annotation { "Feature Type Name" : "Feature", "Feature Type Description" : "" }
export const myFeature = defineFeature(function(context is Context, id is Id, definition is map)
    precondition{}
    {
        {
            var Q0;
            Q0=qCreatedBy(makeId("Top.planeOp"),FACE);
            var sketch = newSketch(context, id + "F0", { "sketchPlane" : qUnion([Q0])});
            skLineSegment(sketch, "E0.bottom", {"start": v(0, -12.7) * mm, "end": v(-66.68, -12.7) * mm});
            skLineSegment(sketch, "E0.top", {"start": v(0, 39.69) * mm, "end": v(-66.68, 39.69) * mm});
            skLineSegment(sketch, "E0.left", {"start": v(0, -12.7) * mm, "end": v(0, 39.69) * mm});
            skLineSegment(sketch, "E0.right", {"start": v(-66.68, -12.7) * mm, "end": v(-66.68, 39.69) * mm});
            skLineSegment(sketch, "E1.right", {"start": v(-69.85, 34.13) * mm, "end": v(-69.85, 3.17) * mm});
            skLineSegment(sketch, "E2", {"start": v(-66.68, 37.3) * mm, "end": v(-69.85, 34.13) * mm});
            skLineSegment(sketch, "E3", {"start": v(-66.68, 0) * mm, "end": v(-69.85, 3.18) * mm});
            skLineSegment(sketch, "E4", {"start": v(-66.68, -11.11) * mm, "end": v(-65.09, -12.7) * mm});
            skCircle(sketch, "E5", {"center": v(-14.29, 37.3) * mm, "radius": 1.59 * mm});
            skCircle(sketch, "E6", {"center": v(-67.47, 31.75) * mm, "radius": 1.59 * mm});
            skCircle(sketch, "E7", {"center": v(-14.29, -10.32) * mm, "radius": 1.59 * mm});
            skCircle(sketch, "E8", {"center": v(-67.47, 5.56) * mm, "radius": 1.59 * mm});
            skLineSegment(sketch, "E9", {"start": v(-69.85, 3.17) * mm, "end": v(-66.68, 3.17) * mm});
            skLineSegment(sketch, "E10", {"start": v(-69.85, 34.13) * mm, "end": v(-66.68, 34.13) * mm});
            skSolve(sketch);
        }
        {
            var Q0;
            {var subQ0=sQuery(id+"F0.wireOp",EDGE,"E3");Q0=makeQuery(id+"F0.imprint","IMPRINT",FACE,{"disambiguationData":[TD([[makeQuery(id+"F0.imprint","IMPRINT",EDGE,{"derivedFrom":subQ0}),-1.0]])]});}
            var Q1;
            {var subQ0=sQuery(id+"F0.wireOp",EDGE,"E2");Q1=makeQuery(id+"F0.imprint","IMPRINT",FACE,{"disambiguationData":[TD([[makeQuery(id+"F0.imprint","IMPRINT",EDGE,{"derivedFrom":subQ0}),1.0]])]});}
            var Q2;
            Q2=makeQuery(id+"F0.imprint","IMPRINT",FACE,{"disambiguationData":[TD([[makeQuery(id+"F0.imprint","IMPRINT",EDGE,{"derivedFrom":sQuery(id+"F0.wireOp",EDGE,"E1.right")}),1.0]])]});
            var Q3;
            {var subQ10=sQuery(id+"F0.wireOp",EDGE,"E0.top");Q3=makeQuery(id+"F0.imprint","IMPRINT",FACE,{"disambiguationData":[TD([[makeQuery(id+"F0.imprint","IMPRINT",EDGE,{"derivedFrom":subQ10}),1.0]])]});}
            extrude(context, id + "F1", {"entities" : qUnion([Q0, Q1, Q2, Q3]), "depth" : 1.59 * mm});
        }
        {
            var Q0;
            Q0=makeQuery(id+"F1.opExtrude","CAP_FACE",FACE,{"disambiguationData":[OSD([sQuery(id+"F0.wireOp",EDGE,"E0.bottom"),sQuery(id+"F0.wireOp",EDGE,"E0.top"),sQuery(id+"F0.wireOp",EDGE,"E0.left"),sQuery(id+"F0.wireOp",EDGE,"E0.right"),sQuery(id+"F0.wireOp",EDGE,"E1.right"),sQuery(id+"F0.wireOp",EDGE,"E2"),sQuery(id+"F0.wireOp",EDGE,"E3"),sQuery(id+"F0.wireOp",EDGE,"E4"),sQuery(id+"F0.wireOp",EDGE,"E5"),sQuery(id+"F0.wireOp",EDGE,"E6"),sQuery(id+"F0.wireOp",EDGE,"E7"),sQuery(id+"F0.wireOp",EDGE,"E8")])],"isStart":true});
            var sketch = newSketch(context, id + "F2", { "sketchPlane" : qUnion([Q0])});
            skPoint(sketch, "E11.secondSnap0", {"position": v(-68.26, -1.59) * mm});
            skText(sketch, "E12", { "text": " His Royal Highness, Lord, Sir Earl, Baron,\n Marquis of the Earth, Gregory Maximus\n Patrick Harrison E.S.B.P. O.B.E. Ph.D M.D\n D.D.S. Duke of Davids House\n\nLord of Canada David Godin ", "fontName": "AllertaStencil-Regular.ttf"});
            const initialGuessF2  = {"E12": [-0.06427, 0, 1, 0, 0.00182]};
            skSetInitialGuess(sketch, initialGuessF2);
            skSolve(sketch);
        }
        {
            var Q0;
            Q0 = qSketchRegion(id + "F2", true);
            var Q1;
            Q1 = qSketchRegion(id + "F2", true);
            extrude(context, id + "F3", {"entities" : qUnion([Q0, Q1]), "operationType" : NewBodyOperationType.ADD, "depth" : 0.03 * mm});
        }
        {
            var Q0;
            Q0=makeQuery(id+"F1.opExtrude","CAP_FACE",FACE,{"disambiguationData":[OSD([sQuery(id+"F0.wireOp",EDGE,"E0.bottom"),sQuery(id+"F0.wireOp",EDGE,"E0.top"),sQuery(id+"F0.wireOp",EDGE,"E0.left"),sQuery(id+"F0.wireOp",EDGE,"E0.right"),sQuery(id+"F0.wireOp",EDGE,"E1.right"),sQuery(id+"F0.wireOp",EDGE,"E2"),sQuery(id+"F0.wireOp",EDGE,"E3"),sQuery(id+"F0.wireOp",EDGE,"E4"),sQuery(id+"F0.wireOp",EDGE,"E5"),sQuery(id+"F0.wireOp",EDGE,"E6"),sQuery(id+"F0.wireOp",EDGE,"E7"),sQuery(id+"F0.wireOp",EDGE,"E8")])],"isStart":false});
            var sketch = newSketch(context, id + "F4", { "sketchPlane" : qUnion([Q0])});
            skLineSegment(sketch, "E13.bottom", {"start": v(-64.14, 38.42) * mm, "end": v(-48.26, 38.42) * mm});
            skLineSegment(sketch, "E13.top", {"start": v(-64.14, 35.88) * mm, "end": v(-48.26, 35.88) * mm});
            skLineSegment(sketch, "E13.left", {"start": v(-64.14, 38.42) * mm, "end": v(-64.14, 35.88) * mm});
            skLineSegment(sketch, "E13.right", {"start": v(-48.26, 38.42) * mm, "end": v(-48.26, 35.88) * mm});
            skLineSegment(sketch, "E14.bottom", {"start": v(-45.72, 38.42) * mm, "end": v(-29.85, 38.42) * mm});
            skLineSegment(sketch, "E14.top", {"start": v(-45.72, 35.88) * mm, "end": v(-29.85, 35.88) * mm});
            skLineSegment(sketch, "E14.left", {"start": v(-45.72, 38.42) * mm, "end": v(-45.72, 35.88) * mm});
            skLineSegment(sketch, "E14.right", {"start": v(-29.85, 38.42) * mm, "end": v(-29.85, 35.88) * mm});
            skLineSegment(sketch, "E15.bottom", {"start": v(-64.14, -8.9) * mm, "end": v(-45.09, -8.9) * mm});
            skLineSegment(sketch, "E15.top", {"start": v(-64.14, -11.43) * mm, "end": v(-45.09, -11.43) * mm});
            skLineSegment(sketch, "E15.left", {"start": v(-64.14, -8.9) * mm, "end": v(-64.14, -11.43) * mm});
            skLineSegment(sketch, "E15.right", {"start": v(-45.09, -8.89) * mm, "end": v(-45.09, -11.43) * mm});
            skLineSegment(sketch, "E16.bottom", {"start": v(-42.55, -8.9) * mm, "end": v(-23.5, -8.89) * mm});
            skLineSegment(sketch, "E16.top", {"start": v(-42.55, -11.43) * mm, "end": v(-23.5, -11.43) * mm});
            skLineSegment(sketch, "E16.left", {"start": v(-42.55, -8.9) * mm, "end": v(-42.55, -11.43) * mm});
            skLineSegment(sketch, "E16.right", {"start": v(-23.5, -8.9) * mm, "end": v(-23.5, -11.43) * mm});
            skSolve(sketch);
        }
        {
            var Q0;
            Q0 = qSketchRegion(id + "F4", true);
            extrude(context, id + "F5", {"entities" : qUnion([Q0]), "operationType" : NewBodyOperationType.ADD, "depth" : 7.94 * mm});
        }
        {
            var Q0;
            Q0=makeQuery(id+"F1.opExtrude","CAP_FACE",FACE,{"disambiguationData":[OSD([sQuery(id+"F0.wireOp",EDGE,"E0.bottom"),sQuery(id+"F0.wireOp",EDGE,"E0.top"),sQuery(id+"F0.wireOp",EDGE,"E0.left"),sQuery(id+"F0.wireOp",EDGE,"E0.right"),sQuery(id+"F0.wireOp",EDGE,"E1.right"),sQuery(id+"F0.wireOp",EDGE,"E2"),sQuery(id+"F0.wireOp",EDGE,"E3"),sQuery(id+"F0.wireOp",EDGE,"E4"),sQuery(id+"F0.wireOp",EDGE,"E5"),sQuery(id+"F0.wireOp",EDGE,"E6"),sQuery(id+"F0.wireOp",EDGE,"E7"),sQuery(id+"F0.wireOp",EDGE,"E8")])],"isStart":false});
            var sketch = newSketch(context, id + "F6", { "sketchPlane" : qUnion([Q0])});
            skCircle(sketch, "E17", {"center": v(-26.42, 35.24) * mm, "radius": 3.18 * mm});
            skCircle(sketch, "E18", {"center": v(-19.56, 35.24) * mm, "radius": 3.18 * mm});
            skSolve(sketch);
        }
        {
            var Q0;
            Q0 = qSketchRegion(id + "F6", true);
            extrude(context, id + "F7", {"entities" : qUnion([Q0]), "operationType" : NewBodyOperationType.ADD, "depth" : 7.94 * mm});
        }
        {
            var Q0;
            Q0=makeQuery(id+"F1.opExtrude","CAP_FACE",FACE,{"disambiguationData":[OSD([sQuery(id+"F0.wireOp",EDGE,"E0.bottom"),sQuery(id+"F0.wireOp",EDGE,"E0.top"),sQuery(id+"F0.wireOp",EDGE,"E0.left"),sQuery(id+"F0.wireOp",EDGE,"E0.right"),sQuery(id+"F0.wireOp",EDGE,"E1.right"),sQuery(id+"F0.wireOp",EDGE,"E2"),sQuery(id+"F0.wireOp",EDGE,"E3"),sQuery(id+"F0.wireOp",EDGE,"E4"),sQuery(id+"F0.wireOp",EDGE,"E5"),sQuery(id+"F0.wireOp",EDGE,"E6"),sQuery(id+"F0.wireOp",EDGE,"E7"),sQuery(id+"F0.wireOp",EDGE,"E8")])],"isStart":false});
            var sketch = newSketch(context, id + "F8", { "sketchPlane" : qUnion([Q0])});
            skLineSegment(sketch, "E19.bottom", {"start": v(-63.88, 29.63) * mm, "end": v(-30.51, 29.63) * mm});
            skLineSegment(sketch, "E19.top", {"start": v(-63.88, 20.5) * mm, "end": v(-30.51, 20.5) * mm});
            skLineSegment(sketch, "E19.left", {"start": v(-63.88, 29.63) * mm, "end": v(-63.88, 20.5) * mm});
            skLineSegment(sketch, "E19.right", {"start": v(-30.51, 29.63) * mm, "end": v(-30.51, 20.5) * mm});
            skSolve(sketch);
        }
        {
            var Q0;
            Q0 = qSketchRegion(id + "F8", true);
            extrude(context, id + "F9", {"entities" : qUnion([Q0]), "operationType" : NewBodyOperationType.ADD, "depth" : 7.94 * mm});
        }
        {
            var Q0;
            Q0=makeQuery(id+"F9.opExtrude","SWEPT_FACE",FACE,{"disambiguationData":[OSD([sQuery(id+"F8.wireOp",EDGE,"E19.right")])]});
            var sketch = newSketch(context, id + "F10", { "sketchPlane" : qUnion([Q0])});
            skLineSegment(sketch, "E20.bottom", {"start": v(22.28, 9.53) * mm, "end": v(27.85, 9.53) * mm});
            skLineSegment(sketch, "E20.top", {"start": v(22.28, 1.59) * mm, "end": v(27.85, 1.59) * mm});
            skLineSegment(sketch, "E20.left", {"start": v(22.28, 9.53) * mm, "end": v(22.28, 1.59) * mm});
            skLineSegment(sketch, "E20.right", {"start": v(27.85, 9.53) * mm, "end": v(27.85, 1.59) * mm});
            skLineSegment(sketch, "E21.bottom", {"start": v(29.63, 7.75) * mm, "end": v(27.85, 7.75) * mm});
            skLineSegment(sketch, "E21.top", {"start": v(29.63, 1.59) * mm, "end": v(27.85, 1.59) * mm});
            skLineSegment(sketch, "E21.left", {"start": v(29.63, 7.75) * mm, "end": v(29.63, 1.59) * mm});
            skLineSegment(sketch, "E21.right", {"start": v(27.85, 7.75) * mm, "end": v(27.85, 1.59) * mm});
            skLineSegment(sketch, "E22.bottom", {"start": v(22.28, 7.75) * mm, "end": v(20.5, 7.75) * mm});
            skLineSegment(sketch, "E22.top", {"start": v(22.28, 1.59) * mm, "end": v(20.5, 1.59) * mm});
            skLineSegment(sketch, "E22.left", {"start": v(22.28, 7.75) * mm, "end": v(22.28, 1.59) * mm});
            skLineSegment(sketch, "E22.right", {"start": v(20.5, 7.75) * mm, "end": v(20.5, 1.59) * mm});
            skCircle(sketch, "E23", {"center": v(22.28, 7.75) * mm, "radius": 1.12 * mm});
            skCircle(sketch, "E24", {"center": v(27.85, 7.75) * mm, "radius": 1.12 * mm});
            skSolve(sketch);
        }
        {
            var Q0;
            {var subQ6=sQuery(id+"F10.wireOp",EDGE,"E23");var subQ7=sQuery(id+"F10.wireOp",EDGE,"E20.left");var subQ8=makeQuery(id+"F10.imprint","INTERSECT",VERTEX,{"derivedFrom":[subQ7,subQ6]});Q0=makeQuery(id+"F10.imprint","IMPRINT",FACE,{"disambiguationData":[TD([[makeQuery(id+"F10.imprint","IMPRINT",EDGE,{"disambiguationData":[TD([[subQ8,-1.0]])],"derivedFrom":subQ6}),-1.0]])]});}
            var Q1;
            {var subQ6=sQuery(id+"F10.wireOp",EDGE,"E24");var subQ7=sQuery(id+"F10.wireOp",EDGE,"E20.right");var subQ8=makeQuery(id+"F10.imprint","INTERSECT",VERTEX,{"derivedFrom":[subQ7,subQ6]});Q1=makeQuery(id+"F10.imprint","IMPRINT",FACE,{"disambiguationData":[TD([[makeQuery(id+"F10.imprint","IMPRINT",EDGE,{"disambiguationData":[TD([[subQ8,1.0]])],"derivedFrom":subQ6}),-1.0]])]});}
            extrude(context, id + "F11", {"entities" : qUnion([Q0, Q1]), "operationType" : NewBodyOperationType.REMOVE, "endBound" : BoundingType.THROUGH_ALL, "oppositeDirection" : true, "depth" : 25.4 * mm});
        }
        {
            var Q0;
            Q0=makeQuery(id+"F1.opExtrude","CAP_FACE",FACE,{"disambiguationData":[OSD([sQuery(id+"F0.wireOp",EDGE,"E0.bottom"),sQuery(id+"F0.wireOp",EDGE,"E0.top"),sQuery(id+"F0.wireOp",EDGE,"E0.left"),sQuery(id+"F0.wireOp",EDGE,"E0.right"),sQuery(id+"F0.wireOp",EDGE,"E1.right"),sQuery(id+"F0.wireOp",EDGE,"E2"),sQuery(id+"F0.wireOp",EDGE,"E3"),sQuery(id+"F0.wireOp",EDGE,"E4"),sQuery(id+"F0.wireOp",EDGE,"E5"),sQuery(id+"F0.wireOp",EDGE,"E6"),sQuery(id+"F0.wireOp",EDGE,"E7"),sQuery(id+"F0.wireOp",EDGE,"E8")])],"isStart":false});
            var sketch = newSketch(context, id + "F12", { "sketchPlane" : qUnion([Q0])});
            skLineSegment(sketch, "E25.bottom", {"start": v(0, 32.38) * mm, "end": v(-2.2, 32.38) * mm});
            skLineSegment(sketch, "E25.top", {"start": v(0, 26.17) * mm, "end": v(-2.2, 26.17) * mm});
            skLineSegment(sketch, "E25.left", {"start": v(0, 32.38) * mm, "end": v(0, 26.17) * mm});
            skLineSegment(sketch, "E25.right", {"start": v(-2.2, 32.38) * mm, "end": v(-2.2, 26.17) * mm});
            skLineSegment(sketch, "E26.bottom", {"start": v(0, 16.83) * mm, "end": v(-3.1, 16.83) * mm});
            skLineSegment(sketch, "E26.top", {"start": v(0, 7.3) * mm, "end": v(-3.1, 7.3) * mm});
            skLineSegment(sketch, "E26.left", {"start": v(0, 16.83) * mm, "end": v(0, 7.3) * mm});
            skLineSegment(sketch, "E26.right", {"start": v(-3.1, 16.83) * mm, "end": v(-3.1, 7.3) * mm});
            skSolve(sketch);
        }
        {
            var Q0;
            Q0 = qSketchRegion(id + "F12", true);
            extrude(context, id + "F13", {"entities" : qUnion([Q0]), "operationType" : NewBodyOperationType.ADD, "depth" : 6.35 * mm});
        }
        {
            var Q0;
            Q0=makeQuery(id+"F13.boolean.opBoolean","MERGE",FACE,{"derivedFrom":[makeQuery(id+"F1.opExtrude","SWEPT_FACE",FACE,{"disambiguationData":[OSD([sQuery(id+"F0.wireOp",EDGE,"E0.left")])]}),makeQuery(id+"F13.opExtrude","SWEPT_FACE",FACE,{"disambiguationData":[OSD([sQuery(id+"F12.wireOp",EDGE,"E25.left")])]}),makeQuery(id+"F13.opExtrude","SWEPT_FACE",FACE,{"disambiguationData":[OSD([sQuery(id+"F12.wireOp",EDGE,"E26.left")])]})]});
            var sketch = newSketch(context, id + "F14", { "sketchPlane" : qUnion([Q0])});
            skLineSegment(sketch, "E27.bottom", {"start": v(26.13, 0) * mm, "end": v(32.48, 0) * mm});
            skLineSegment(sketch, "E27.top", {"start": v(26.13, 8) * mm, "end": v(32.48, 8) * mm});
            skLineSegment(sketch, "E27.left", {"start": v(26.13, 0) * mm, "end": v(26.13, 8) * mm});
            skLineSegment(sketch, "E27.right", {"start": v(32.48, 0) * mm, "end": v(32.48, 8) * mm});
            skLineSegment(sketch, "E28", {"start": v(26.17, 1.59) * mm, "end": v(32.38, 1.59) * mm});
            skSolve(sketch);
        }
        {
            var Q0;
            Q0=makeQuery(id+"F14.imprint","IMPRINT",FACE,{"disambiguationData":[TD([[makeQuery(id+"F14.imprint","IMPRINT",EDGE,{"derivedFrom":sQuery(id+"F14.wireOp",EDGE,"E28")}),1.0]])]});
            extrude(context, id + "F15", {"entities" : qUnion([Q0]), "operationType" : NewBodyOperationType.ADD, "depth" : 1.59 * mm});
        }
        {
            var Q0;
            Q0=makeQuery(id+"F13.opExtrude","SWEPT_FACE",FACE,{"disambiguationData":[OSD([sQuery(id+"F12.wireOp",EDGE,"E25.right")])]});
            var sketch = newSketch(context, id + "F16", { "sketchPlane" : qUnion([Q0])});
            skLineSegment(sketch, "E29", {"start": v(-32.38, 7.94) * mm, "end": v(-26.17, 7.94) * mm});
            skCircle(sketch, "E30", {"center": v(-29.2, 4.76) * mm, "radius": 3.18 * mm});
            skPoint(sketch, "E30.first.point", {"position": v(-29.28, 7.94) * mm});
            skPoint(sketch, "E30.second.point", {"position": v(-29.28, 1.59) * mm});
            skPoint(sketch, "E30.third.point", {"position": v(-32.38, 4.76) * mm});
            skLineSegment(sketch, "E31.bottom", {"start": v(-29.2, 4.76) * mm, "end": v(-32.38, 4.76) * mm});
            skLineSegment(sketch, "E31.top", {"start": v(-29.2, 1.59) * mm, "end": v(-32.38, 1.59) * mm});
            skLineSegment(sketch, "E31.left", {"start": v(-29.2, 4.76) * mm, "end": v(-29.2, 1.59) * mm});
            skLineSegment(sketch, "E31.right", {"start": v(-32.38, 4.76) * mm, "end": v(-32.38, 1.59) * mm});
            skLineSegment(sketch, "E32.bottom", {"start": v(-29.2, 4.76) * mm, "end": v(-26.17, 4.76) * mm});
            skLineSegment(sketch, "E32.top", {"start": v(-29.2, 1.59) * mm, "end": v(-26.17, 1.59) * mm});
            skLineSegment(sketch, "E32.right", {"start": v(-26.17, 4.76) * mm, "end": v(-26.17, 1.59) * mm});
            skSolve(sketch);
        }
        {
            var Q0;
            Q0 = qSketchRegion(id + "F16", true);
            extrude(context, id + "F17", {"entities" : qUnion([Q0]), "operationType" : NewBodyOperationType.ADD, "depth" : 6.35 * mm});
        }
        {
            var Q0;
            Q0=makeQuery(id+"F15.opExtrude","CAP_FACE",FACE,{"disambiguationData":[OSD([sQuery(id+"F0.wireOp",EDGE,"E0.left"),sQuery(id+"F12.wireOp",EDGE,"E25.bottom"),sQuery(id+"F12.wireOp",EDGE,"E25.top"),sQuery(id+"F12.wireOp",EDGE,"E25.left"),sQuery(id+"F14.wireOp",EDGE,"E28")])],"isStart":false});
            var sketch = newSketch(context, id + "F18", { "sketchPlane" : qUnion([Q0])});
            skLineSegment(sketch, "E33", {"start": v(26.17, 7.94) * mm, "end": v(26.17, 1.59) * mm, "construction": true});
            skLineSegment(sketch, "E34", {"start": v(26.17, 1.59) * mm, "end": v(32.38, 1.59) * mm, "construction": true});
            skLineSegment(sketch, "E35", {"start": v(32.38, 1.59) * mm, "end": v(32.38, 7.94) * mm, "construction": true});
            skLineSegment(sketch, "E36", {"start": v(32.38, 7.94) * mm, "end": v(26.17, 7.94) * mm, "construction": true});
            skLineSegment(sketch, "E37", {"start": v(26.17, 4.76) * mm, "end": v(32.38, 4.76) * mm});
            skLineSegment(sketch, "E38", {"start": v(29.28, 7.94) * mm, "end": v(29.28, 1.59) * mm});
            skCircle(sketch, "E39", {"center": v(29.28, 4.76) * mm, "radius": 2.27 * mm});
            skCircle(sketch, "E40", {"center": v(29.28, 4.76) * mm, "radius": 0.59 * mm});
            skSolve(sketch);
        }
        {
            var Q0;
            Q0 = qSketchRegion(id + "F18", true);
            extrude(context, id + "F19", {"entities" : qUnion([Q0]), "operationType" : NewBodyOperationType.REMOVE, "oppositeDirection" : true, "depth" : 6.35 * mm});
        }
        {
            var Q0;
            Q0=makeQuery(id+"F13.opExtrude","CAP_FACE",FACE,{"disambiguationData":[OSD([sQuery(id+"F12.wireOp",EDGE,"E26.bottom"),sQuery(id+"F12.wireOp",EDGE,"E26.top"),sQuery(id+"F12.wireOp",EDGE,"E26.left"),sQuery(id+"F12.wireOp",EDGE,"E26.right")])],"isStart":false});
            var sketch = newSketch(context, id + "F20", { "sketchPlane" : qUnion([Q0])});
            skPoint(sketch, "E41.firstSnap0", {"position": v(-1.55, 7.3) * mm});
            skLineSegment(sketch, "E41.bottom", {"start": v(-1.55, 11.06) * mm, "end": v(-0.78, 11.06) * mm});
            skLineSegment(sketch, "E41.top", {"start": v(-1.55, 8.03) * mm, "end": v(-0.78, 8.03) * mm});
            skLineSegment(sketch, "E41.left", {"start": v(-1.55, 11.06) * mm, "end": v(-1.55, 8.03) * mm});
            skLineSegment(sketch, "E41.right", {"start": v(-0.78, 11.06) * mm, "end": v(-0.78, 8.03) * mm});
            skLineSegment(sketch, "E42", {"start": v(-1.55, 7.3) * mm, "end": v(-1.55, 16.83) * mm, "construction": true});
            skLineSegment(sketch, "E43.bottom", {"start": v(-1.55, 11.06) * mm, "end": v(-2.32, 11.06) * mm});
            skLineSegment(sketch, "E43.top", {"start": v(-1.55, 8.03) * mm, "end": v(-2.32, 8.03) * mm});
            skLineSegment(sketch, "E43.right", {"start": v(-2.32, 11.06) * mm, "end": v(-2.32, 8.03) * mm});
            skSolve(sketch);
        }
        {
            var Q0;
            Q0=makeQuery(id+"F1.opExtrude","CAP_FACE",FACE,{"disambiguationData":[OSD([sQuery(id+"F0.wireOp",EDGE,"E0.bottom"),sQuery(id+"F0.wireOp",EDGE,"E0.top"),sQuery(id+"F0.wireOp",EDGE,"E0.left"),sQuery(id+"F0.wireOp",EDGE,"E0.right"),sQuery(id+"F0.wireOp",EDGE,"E1.right"),sQuery(id+"F0.wireOp",EDGE,"E2"),sQuery(id+"F0.wireOp",EDGE,"E3"),sQuery(id+"F0.wireOp",EDGE,"E4"),sQuery(id+"F0.wireOp",EDGE,"E5"),sQuery(id+"F0.wireOp",EDGE,"E6"),sQuery(id+"F0.wireOp",EDGE,"E7"),sQuery(id+"F0.wireOp",EDGE,"E8")])],"isStart":false});
            var sketch = newSketch(context, id + "F21", { "sketchPlane" : qUnion([Q0])});
            skLineSegment(sketch, "E44.bottom", {"start": v(0, -5.18) * mm, "end": v(-0.7, -5.18) * mm});
            skLineSegment(sketch, "E44.top", {"start": v(0, -0.5) * mm, "end": v(-0.7, -0.5) * mm});
            skLineSegment(sketch, "E44.left", {"start": v(0, -5.18) * mm, "end": v(0, -0.5) * mm});
            skLineSegment(sketch, "E44.right", {"start": v(-0.7, -5.18) * mm, "end": v(-0.7, -0.5) * mm});
            skSolve(sketch);
        }
        {
            var Q0;
            Q0 = qSketchRegion(id + "F21", true);
            extrude(context, id + "F22", {"entities" : qUnion([Q0]), "operationType" : NewBodyOperationType.ADD, "depth" : 1.59 * mm});
        }
        {
            var Q0;
            Q0 = qSketchRegion(id + "F20", true);
            extrude(context, id + "F23", {"entities" : qUnion([Q0]), "operationType" : NewBodyOperationType.ADD, "depth" : 1.59 * mm});
        }
        {
            var Q0;
            Q0=makeQuery(id+"F22.boolean.opBoolean","MERGE",FACE,{"derivedFrom":[makeQuery(id+"F13.boolean.opBoolean","MERGE",FACE,{"derivedFrom":[makeQuery(id+"F1.opExtrude","SWEPT_FACE",FACE,{"disambiguationData":[OSD([sQuery(id+"F0.wireOp",EDGE,"E0.left")])]}),makeQuery(id+"F13.opExtrude","SWEPT_FACE",FACE,{"disambiguationData":[OSD([sQuery(id+"F12.wireOp",EDGE,"E25.left")])]}),makeQuery(id+"F13.opExtrude","SWEPT_FACE",FACE,{"disambiguationData":[OSD([sQuery(id+"F12.wireOp",EDGE,"E26.left")])]})]}),makeQuery(id+"F22.opExtrude","SWEPT_FACE",FACE,{"disambiguationData":[OSD([sQuery(id+"F21.wireOp",EDGE,"E44.left")])]})]});
            var sketch = newSketch(context, id + "F24", { "sketchPlane" : qUnion([Q0])});
            skLineSegment(sketch, "E45", {"start": v(-5.7, 4.66) * mm, "end": v(1.1, 4.66) * mm});
            skArc(sketch, "E46", {"start": v(1.1, 3.16) * mm, "mid": v(1.85, 3.91) * mm, "end": v(1.1, 4.66) * mm});
            skArc(sketch, "E47", {"start": v(1.1, 3.16) * mm, "mid": v(0.53, 3) * mm, "end": v(0.46, 2.41) * mm});
            skLineSegment(sketch, "E48", {"start": v(0.46, 2.41) * mm, "end": v(0.46, 1.59) * mm});
            skLineSegment(sketch, "E49", {"start": v(-5.18, 1.59) * mm, "end": v(-0.5, 1.59) * mm, "construction": true});
            skLineSegment(sketch, "E50", {"start": v(-0.5, 1.59) * mm, "end": v(-2.84, 1.59) * mm, "construction": true});
            skLineSegment(sketch, "E51", {"start": v(-2.84, 1.59) * mm, "end": v(-2.84, 4.66) * mm, "construction": true});
            skPoint(sketch, "E51.endSnap0", {"position": v(-2.84, 3.18) * mm});
            skLineSegment(sketch, "E52.MirrorCS", {"start": v(0.02, 4.66) * mm, "end": v(-6.78, 4.66) * mm});
            skLineSegment(sketch, "E53.MirrorCS", {"start": v(-6.15, 2.41) * mm, "end": v(-6.15, 1.59) * mm});
            skArc(sketch, "E54.MirrorCS", {"start": v(-6.78, 3.16) * mm, "mid": v(-6.22, 3) * mm, "end": v(-6.15, 2.41) * mm});
            skArc(sketch, "E55.MirrorCS", {"start": v(-6.78, 3.16) * mm, "mid": v(-7.53, 3.91) * mm, "end": v(-6.78, 4.66) * mm});
            skLineSegment(sketch, "E56", {"start": v(-6.15, 1.59) * mm, "end": v(0.46, 1.59) * mm});
            skSolve(sketch);
        }
        {
            var Q0;
            Q0 = qSketchRegion(id + "F24", true);
            extrude(context, id + "F25", {"entities" : qUnion([Q0]), "operationType" : NewBodyOperationType.ADD, "oppositeDirection" : true, "depth" : 9.52 * mm});
        }
        {
            var Q0;
            Q0=makeQuery(id+"F25.boolean.opBoolean","MERGE",FACE,{"derivedFrom":[makeQuery(id+"F22.boolean.opBoolean","MERGE",FACE,{"derivedFrom":[makeQuery(id+"F13.boolean.opBoolean","MERGE",FACE,{"derivedFrom":[makeQuery(id+"F1.opExtrude","SWEPT_FACE",FACE,{"disambiguationData":[OSD([sQuery(id+"F0.wireOp",EDGE,"E0.left")])]}),makeQuery(id+"F13.opExtrude","SWEPT_FACE",FACE,{"disambiguationData":[OSD([sQuery(id+"F12.wireOp",EDGE,"E25.left")])]}),makeQuery(id+"F13.opExtrude","SWEPT_FACE",FACE,{"disambiguationData":[OSD([sQuery(id+"F12.wireOp",EDGE,"E26.left")])]})]}),makeQuery(id+"F22.opExtrude","SWEPT_FACE",FACE,{"disambiguationData":[OSD([sQuery(id+"F21.wireOp",EDGE,"E44.left")])]})]}),makeQuery(id+"F25.opExtrude","CAP_FACE",FACE,{"disambiguationData":[OSD([sQuery(id+"F24.wireOp",EDGE,"E45"),sQuery(id+"F24.wireOp",EDGE,"E46"),sQuery(id+"F24.wireOp",EDGE,"E47"),sQuery(id+"F24.wireOp",EDGE,"E48"),sQuery(id+"F24.wireOp",EDGE,"E52.MirrorCS"),sQuery(id+"F24.wireOp",EDGE,"E53.MirrorCS"),sQuery(id+"F24.wireOp",EDGE,"E54.MirrorCS"),sQuery(id+"F24.wireOp",EDGE,"E55.MirrorCS"),sQuery(id+"F24.wireOp",EDGE,"E56")])],"isStart":true})]});
            var sketch = newSketch(context, id + "F26", { "sketchPlane" : qUnion([Q0])});
            skLineSegment(sketch, "E57", {"start": v(-6.15, 4.33) * mm, "end": v(0.97, 4.33) * mm});
            skLineSegment(sketch, "E58", {"start": v(-6.15, 2.41) * mm, "end": v(0.46, 2.41) * mm, "construction": true});
            skLineSegment(sketch, "E59", {"start": v(0.46, 2.41) * mm, "end": v(-2.84, 2.41) * mm, "construction": true});
            skLineSegment(sketch, "E60", {"start": v(-2.84, 2.41) * mm, "end": v(-2.84, 4.33) * mm, "construction": true});
            skPoint(sketch, "E60.endSnap0", {"position": v(-2.84, 4.66) * mm});
            skArc(sketch, "E61", {"start": v(0.97, 3.62) * mm, "mid": v(1.33, 3.97) * mm, "end": v(0.97, 4.33) * mm, "construction": true});
            skArc(sketch, "E62", {"start": v(0.97, 3.62) * mm, "mid": v(0.32, 3.55) * mm, "end": v(0.2, 2.9) * mm, "construction": true});
            skLineSegment(sketch, "E63", {"start": v(0.2, 2.9) * mm, "end": v(-2.84, 2.9) * mm});
            skArc(sketch, "E64", {"start": v(0.97, 3.62) * mm, "mid": v(0.35, 3.51) * mm, "end": v(0.2, 2.9) * mm});
            skArc(sketch, "E65", {"start": v(0.97, 3.62) * mm, "mid": v(1.33, 3.97) * mm, "end": v(0.97, 4.33) * mm});
            skLineSegment(sketch, "E66.bottom", {"start": v(-2.84, 3.8) * mm, "end": v(-0.93, 3.8) * mm});
            skLineSegment(sketch, "E66.top", {"start": v(-2.84, 3.43) * mm, "end": v(-0.93, 3.43) * mm});
            skLineSegment(sketch, "E66.left", {"start": v(-2.84, 3.8) * mm, "end": v(-2.84, 3.43) * mm});
            skLineSegment(sketch, "E66.right", {"start": v(-0.93, 3.8) * mm, "end": v(-0.93, 3.43) * mm});
            skLineSegment(sketch, "E67.MirrorCS", {"start": v(0.46, 4.33) * mm, "end": v(-6.66, 4.33) * mm});
            skArc(sketch, "E68.MirrorCS", {"start": v(-6.66, 3.62) * mm, "mid": v(-6.04, 3.51) * mm, "end": v(-5.88, 2.9) * mm});
            skArc(sketch, "E69.MirrorCS", {"start": v(-6.66, 3.62) * mm, "mid": v(-7.02, 3.97) * mm, "end": v(-6.66, 4.33) * mm});
            skLineSegment(sketch, "E70.MirrorCS", {"start": v(-5.88, 2.9) * mm, "end": v(-2.84, 2.9) * mm});
            skLineSegment(sketch, "E71.MirrorCS", {"start": v(-2.84, 3.43) * mm, "end": v(-4.76, 3.43) * mm});
            skLineSegment(sketch, "E72.MirrorCS", {"start": v(-2.84, 3.8) * mm, "end": v(-4.76, 3.8) * mm});
            skLineSegment(sketch, "E73.MirrorCS", {"start": v(-4.76, 3.8) * mm, "end": v(-4.76, 3.43) * mm});
            skSolve(sketch);
        }
        {
            var Q0;
            Q0 = qSketchRegion(id + "F26", true);
            extrude(context, id + "F27", {"entities" : qUnion([Q0]), "operationType" : NewBodyOperationType.REMOVE, "oppositeDirection" : true, "depth" : 6.1 * mm});
        }
        {
            var Q0;
            Q0=makeQuery(id+"F1.opExtrude","CAP_FACE",FACE,{"disambiguationData":[OSD([sQuery(id+"F0.wireOp",EDGE,"E0.bottom"),sQuery(id+"F0.wireOp",EDGE,"E0.top"),sQuery(id+"F0.wireOp",EDGE,"E0.left"),sQuery(id+"F0.wireOp",EDGE,"E0.right"),sQuery(id+"F0.wireOp",EDGE,"E1.right"),sQuery(id+"F0.wireOp",EDGE,"E2"),sQuery(id+"F0.wireOp",EDGE,"E3"),sQuery(id+"F0.wireOp",EDGE,"E4"),sQuery(id+"F0.wireOp",EDGE,"E5"),sQuery(id+"F0.wireOp",EDGE,"E6"),sQuery(id+"F0.wireOp",EDGE,"E7"),sQuery(id+"F0.wireOp",EDGE,"E8")])],"isStart":false});
            var sketch = newSketch(context, id + "F28", { "sketchPlane" : qUnion([Q0])});
            skLineSegment(sketch, "E74.bottom", {"start": v(-59.3, 16.97) * mm, "end": v(-54.72, 16.97) * mm});
            skLineSegment(sketch, "E74.top", {"start": v(-59.3, 12.4) * mm, "end": v(-54.72, 12.4) * mm});
            skLineSegment(sketch, "E74.left", {"start": v(-59.3, 16.97) * mm, "end": v(-59.3, 12.4) * mm});
            skLineSegment(sketch, "E74.right", {"start": v(-54.72, 16.97) * mm, "end": v(-54.72, 12.4) * mm});
            skSolve(sketch);
        }
        {
            var Q0;
            Q0 = qSketchRegion(id + "F28", true);
            extrude(context, id + "F29", {"entities" : qUnion([Q0]), "operationType" : NewBodyOperationType.ADD, "depth" : 2.54 * mm});
        }
        {
            var Q0;
            Q0=makeQuery(id+"F29.opExtrude","CAP_FACE",FACE,{"disambiguationData":[OSD([sQuery(id+"F28.wireOp",EDGE,"E74.bottom"),sQuery(id+"F28.wireOp",EDGE,"E74.top"),sQuery(id+"F28.wireOp",EDGE,"E74.left"),sQuery(id+"F28.wireOp",EDGE,"E74.right")])],"isStart":false});
            var sketch = newSketch(context, id + "F30", { "sketchPlane" : qUnion([Q0])});
            skLineSegment(sketch, "E75", {"start": v(-59.3, 16.97) * mm, "end": v(-54.72, 16.97) * mm, "construction": true});
            skLineSegment(sketch, "E76", {"start": v(-54.72, 16.97) * mm, "end": v(-54.72, 12.4) * mm, "construction": true});
            skLineSegment(sketch, "E77", {"start": v(-54.72, 12.4) * mm, "end": v(-59.3, 12.4) * mm, "construction": true});
            skLineSegment(sketch, "E78", {"start": v(-59.3, 12.4) * mm, "end": v(-59.3, 16.97) * mm, "construction": true});
            skLineSegment(sketch, "E79", {"start": v(-57.01, 16.97) * mm, "end": v(-57.01, 12.4) * mm, "construction": true});
            skLineSegment(sketch, "E80", {"start": v(-57.01, 12.4) * mm, "end": v(-59.3, 12.4) * mm, "construction": true});
            skLineSegment(sketch, "E81", {"start": v(-59.3, 14.69) * mm, "end": v(-54.72, 14.69) * mm, "construction": true});
            skCircle(sketch, "E82", {"center": v(-57.01, 14.69) * mm, "radius": 1.35 * mm});
            skSolve(sketch);
        }
        {
            var Q0;
            Q0 = qSketchRegion(id + "F30", true);
            extrude(context, id + "F31", {"entities" : qUnion([Q0]), "operationType" : NewBodyOperationType.ADD, "depth" : 2.03 * mm});
        }
        {
            var Q0;
            {var subQ0=sQuery(id+"F24.wireOp",EDGE,"E55.MirrorCS");var subQ2=sQuery(id+"F24.wireOp",EDGE,"E54.MirrorCS");var subQ3=sQuery(id+"F24.wireOp",EDGE,"E53.MirrorCS");var subQ4=sQuery(id+"F24.wireOp",EDGE,"E48");var subQ5=sQuery(id+"F24.wireOp",EDGE,"E47");var subQ6=sQuery(id+"F24.wireOp",EDGE,"E52.MirrorCS");var subQ7=sQuery(id+"F24.wireOp",EDGE,"E45");var subQ8=sQuery(id+"F12.wireOp",EDGE,"E25.left");var subQ9=sQuery(id+"F0.wireOp",EDGE,"E0.left");var subQ20=sQuery(id+"F0.wireOp",EDGE,"E0.bottom");var subQ22=sQuery(id+"F24.wireOp",EDGE,"E46");var subQ24=sQuery(id+"F12.wireOp",EDGE,"E26.left");Q0=makeQuery(id+"F27.boolean.opBoolean","SPLIT",FACE,{"disambiguationData":[TD([makeQuery(id+"F1.opExtrude","SWEPT_FACE",FACE,{"disambiguationData":[OSD([subQ20])]})])],"derivedFrom":makeQuery(id+"F25.boolean.opBoolean","MERGE",FACE,{"derivedFrom":[makeQuery(id+"F22.boolean.opBoolean","MERGE",FACE,{"derivedFrom":[makeQuery(id+"F13.boolean.opBoolean","MERGE",FACE,{"derivedFrom":[makeQuery(id+"F1.opExtrude","SWEPT_FACE",FACE,{"disambiguationData":[OSD([subQ9])]}),makeQuery(id+"F13.opExtrude","SWEPT_FACE",FACE,{"disambiguationData":[OSD([subQ8])]}),makeQuery(id+"F13.opExtrude","SWEPT_FACE",FACE,{"disambiguationData":[OSD([subQ24])]})]}),makeQuery(id+"F22.opExtrude","SWEPT_FACE",FACE,{"disambiguationData":[OSD([sQuery(id+"F21.wireOp",EDGE,"E44.left")])]})]}),makeQuery(id+"F25.opExtrude","CAP_FACE",FACE,{"disambiguationData":[OSD([subQ7,subQ22,subQ5,subQ4,subQ6,subQ3,subQ2,subQ0,sQuery(id+"F24.wireOp",EDGE,"E56")])],"isStart":true})]})});}
            var sketch = newSketch(context, id + "F32", { "sketchPlane" : qUnion([Q0])});
            skLineSegment(sketch, "E83", {"start": v(-6.15, 1.59) * mm, "end": v(0.46, 1.59) * mm});
            skArc(sketch, "E84", {"start": v(1.1, 3.16) * mm, "mid": v(1.85, 3.91) * mm, "end": v(1.1, 4.66) * mm});
            skArc(sketch, "E85", {"start": v(1.1, 3.16) * mm, "mid": v(0.54, 3) * mm, "end": v(0.46, 2.41) * mm});
            skLineSegment(sketch, "E86", {"start": v(0.46, 2.41) * mm, "end": v(0.46, 1.59) * mm});
            skLineSegment(sketch, "E87", {"start": v(-2.84, 4.66) * mm, "end": v(1.1, 4.66) * mm});
            skLineSegment(sketch, "E88", {"start": v(0.46, 1.59) * mm, "end": v(-2.84, 1.59) * mm});
            skPoint(sketch, "E88.endSnap0", {"position": v(-2.84, 2.9) * mm});
            skLineSegment(sketch, "E89", {"start": v(-2.84, 1.59) * mm, "end": v(-2.84, 4.66) * mm, "construction": true});
            skLineSegment(sketch, "E90", {"start": v(-2.84, 4.33) * mm, "end": v(0.97, 4.33) * mm});
            skArc(sketch, "E91", {"start": v(0.97, 3.62) * mm, "mid": v(1.33, 3.97) * mm, "end": v(0.97, 4.33) * mm});
            skArc(sketch, "E92", {"start": v(0.97, 3.62) * mm, "mid": v(0.34, 3.52) * mm, "end": v(0.2, 2.9) * mm});
            skArc(sketch, "E93.MirrorCS", {"start": v(-6.66, 3.62) * mm, "mid": v(-6.03, 3.52) * mm, "end": v(-5.88, 2.9) * mm});
            skArc(sketch, "E94.MirrorCS", {"start": v(-6.78, 3.16) * mm, "mid": v(-6.23, 3) * mm, "end": v(-6.15, 2.41) * mm});
            skLineSegment(sketch, "E95.MirrorCS", {"start": v(-6.15, 2.41) * mm, "end": v(-6.15, 1.59) * mm});
            skLineSegment(sketch, "E96.MirrorCS", {"start": v(-6.15, 1.59) * mm, "end": v(-2.84, 1.59) * mm});
            skLineSegment(sketch, "E97.MirrorCS", {"start": v(-2.84, 4.66) * mm, "end": v(-6.78, 4.66) * mm});
            skArc(sketch, "E98.MirrorCS", {"start": v(-6.66, 3.62) * mm, "mid": v(-7.02, 3.97) * mm, "end": v(-6.66, 4.33) * mm});
            skLineSegment(sketch, "E99.MirrorCS", {"start": v(-2.84, 4.33) * mm, "end": v(-6.66, 4.33) * mm});
            skArc(sketch, "E100.MirrorCS", {"start": v(-6.78, 3.16) * mm, "mid": v(-7.53, 3.91) * mm, "end": v(-6.78, 4.66) * mm});
            skLineSegment(sketch, "E101", {"start": v(-5.88, 2.9) * mm, "end": v(0.2, 2.9) * mm});
            skSolve(sketch);
        }
        {
            var Q0;
            Q0 = qSketchRegion(id + "F32", true);
            extrude(context, id + "F33", {"entities" : qUnion([Q0]), "operationType" : NewBodyOperationType.ADD, "depth" : 1.59 * mm});
        }
        {
            var Q0;
            Q0=makeQuery(id+"F1.opExtrude","SWEPT_BODY",BODY,{"disambiguationData":[OSD([sQuery(id+"F0.wireOp",EDGE,"E0.bottom"),sQuery(id+"F0.wireOp",EDGE,"E0.top"),sQuery(id+"F0.wireOp",EDGE,"E0.left"),sQuery(id+"F0.wireOp",EDGE,"E0.right"),sQuery(id+"F0.wireOp",EDGE,"E1.right"),sQuery(id+"F0.wireOp",EDGE,"E2"),sQuery(id+"F0.wireOp",EDGE,"E3"),sQuery(id+"F0.wireOp",EDGE,"E4"),sQuery(id+"F0.wireOp",EDGE,"E5"),sQuery(id+"F0.wireOp",EDGE,"E6"),sQuery(id+"F0.wireOp",EDGE,"E7"),sQuery(id+"F0.wireOp",EDGE,"E8")])]});
            transform(context, id + "F34", {"entities" : qUnion([Q0]), "transformType" : TransformType.TRANSLATION_3D, "dx" : 0 * mm, "dy" : 0 * mm, "dz" : 0 * mm, "makeCopy" : true});
        }
    });